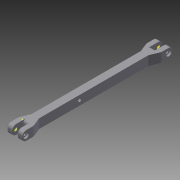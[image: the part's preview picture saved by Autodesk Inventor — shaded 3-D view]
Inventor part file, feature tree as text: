
AUTODESK INVENTOR PART (.ipt)
format: ipt  version: 2015 (Build 190159000, 159)  size: 181,248 bytes
history: native  units: mm
features: sketch x6, fillet x4, extrude x2, plane x2, hole x2, mirror x2, loft x1, other x1
ambient origin geometry x8: Origin, YZ Plane, XZ Plane, XY Plane, X Axis, Y Axis, Z Axis, Center Point
bodies: Solid1 (feature_tree)
feature tree (20):
  extrude  "Extrusion1"  Depth=10.0mm
  sketch  "Sketch2"  dims[d2=138.0mm d3=0.0mm d4=5.0mm]
  sketch  "Sketch3"  dims[d5=5.0mm d6=3.05mm d7=3.05mm d8=10.0mm]
  extrude  "Extrusion3"  Depth=5.0mm
  loft  "Loft2"
  plane  "Work Plane2"
  fillet  "Fillet4"  Radius=3.05mm
  fillet  "Fillet5"  Radius=10.0mm
  hole  "Hole1"  [1 undecoded]
  mirror  "Mirror2"
  plane  "Work Plane3"
  mirror  "Mirror3"
  fillet  "Fillet6"  [1 undecoded]
  fillet  "Fillet7"  Radius=4.0mm
  sketch  "Sketch8"  dims[d25=4.0mm]
  hole  "Hole3"  [1 undecoded]
  sketch  "Sketch1"  dims[d0=8.0mm d1=10.0mm]
  other  "Edges1"
  sketch  "Sketch5"  dims[d18=12.0mm d19=0.0mm d20=0.0mm d21=90.0deg d22=0.0mm d23=90.0deg d24=4.0mm]
  sketch  "Sketch9"  dims[d26=3.3mm d27=6.0mm d28=6.0mm d29=2.0mm d30=90.0deg d31=8.0mm d32=20.594885mm d42=3.0mm d43=3.0mm d44=15.0mm d45=3.3mm d46=6.0mm d47=8.0mm d48=5.0mm d49=90.0deg d50=8.0mm d51=20.594885mm]
note: 3 required parameter values undecoded (feature->parameter linkage not recoverable at this tier; creation-order binding heuristic only, values carry confidence <= 0.55)
